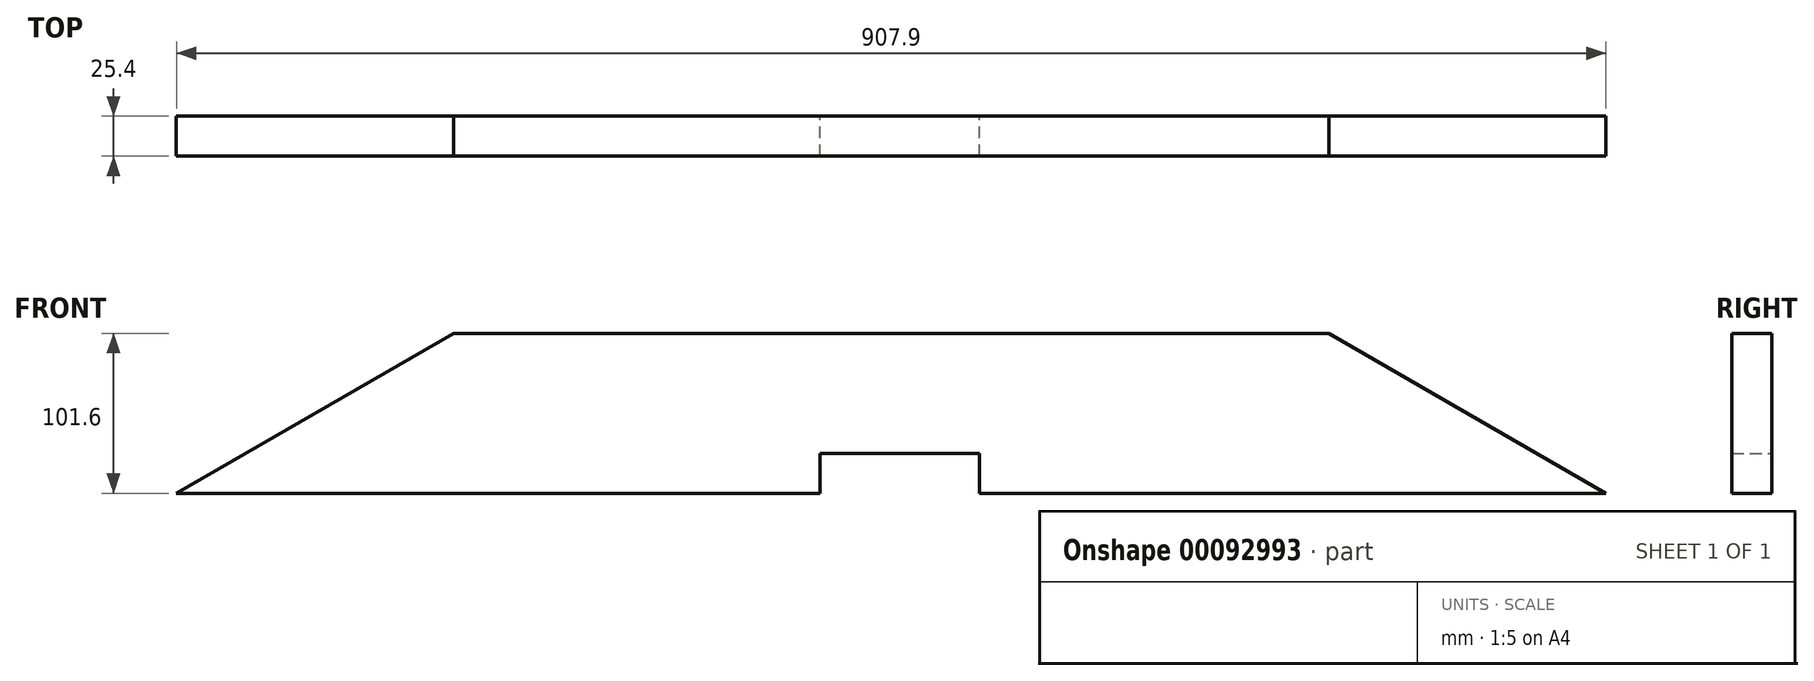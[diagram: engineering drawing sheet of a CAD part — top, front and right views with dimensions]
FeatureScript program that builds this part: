
annotation { "Feature Type Name" : "Feature", "Feature Type Description" : "" }
export const myFeature = defineFeature(function(context is Context, id is Id, definition is map)
    precondition{}
    {
        {
            var Q0;
            Q0=qCreatedBy(makeId("Front.planeOp"),FACE);
            var sketch = newSketch(context, id + "F0", { "sketchPlane" : qUnion([Q0])});
            skLineSegment(sketch, "E0", {"start": v(-1250, 0) * mm, "end": v(1250, 0) * mm, "construction": true});
            skLineSegment(sketch, "E1", {"start": v(-1250, 0) * mm, "end": v(0, 721.69) * mm, "construction": true});
            skLineSegment(sketch, "E2", {"start": v(0, 721.69) * mm, "end": v(1250, 0) * mm, "construction": true});
            skLineSegment(sketch, "E3", {"start": v(-1732.05, -278.31) * mm, "end": v(-1681.25, -366.3) * mm});
            skLineSegment(sketch, "E4", {"start": v(-1681.25, -366.3) * mm, "end": v(0, 604.37) * mm});
            skLineSegment(sketch, "E5", {"start": v(-1732.05, -278.31) * mm, "end": v(0, 721.69) * mm});
            skLineSegment(sketch, "E6", {"start": v(0, 721.69) * mm, "end": v(0, 604.37) * mm});
            skSolve(sketch);
        }
        {
            var Q0;
            Q0=qCreatedBy(makeId("Front.planeOp"),FACE);
            var sketch = newSketch(context, id + "F1", { "sketchPlane" : qUnion([Q0])});
            skLineSegment(sketch, "E7.0", {"start": v(-1250, 0) * mm, "end": v(1250, 0) * mm, "construction": true});
            skLineSegment(sketch, "E8", {"start": v(-459.63, 339) * mm, "end": v(448.27, 339) * mm});
            skLineSegment(sketch, "E9", {"start": v(448.27, 339) * mm, "end": v(272.3, 440.6) * mm});
            skLineSegment(sketch, "E10", {"start": v(272.3, 440.6) * mm, "end": v(-283.66, 440.6) * mm});
            skLineSegment(sketch, "E11.trimOffspring", {"start": v(-459.63, 339) * mm, "end": v(-283.66, 440.6) * mm});
            skSolve(sketch);
        }
        {
            var Q0;
            Q0=makeQuery(id+"F1.imprint","IMPRINT",FACE,{"disambiguationData":[TD([[makeQuery(id+"F1.imprint","IMPRINT",EDGE,{"derivedFrom":sQuery(id+"F1.wireOp",EDGE,"E8")}),1.0]])]});
            extrude(context, id + "F2", {"entities" : qUnion([Q0]), "endBound" : BoundingType.SYMMETRIC, "depth" : 25.4 * mm});
        }
        {
            var Q0;
            Q0=qCreatedBy(makeId("Front.planeOp"),FACE);
            var sketch = newSketch(context, id + "F3", { "sketchPlane" : qUnion([Q0])});
            skLineSegment(sketch, "E12.bottom", {"start": v(-51, 364.4) * mm, "end": v(50.6, 364.4) * mm});
            skLineSegment(sketch, "E12.top", {"start": v(-51, 339) * mm, "end": v(50.6, 339) * mm});
            skLineSegment(sketch, "E12.left", {"start": v(-51, 364.4) * mm, "end": v(-51, 339) * mm});
            skLineSegment(sketch, "E12.right", {"start": v(50.6, 364.4) * mm, "end": v(50.6, 339) * mm});
            skSolve(sketch);
        }
        {
            var Q0;
            Q0 = qSketchRegion(id + "F3", true);
            extrude(context, id + "F4", {"entities" : qUnion([Q0]), "operationType" : NewBodyOperationType.REMOVE, "endBound" : BoundingType.SYMMETRIC, "depth" : 100 * mm});
        }
    });
